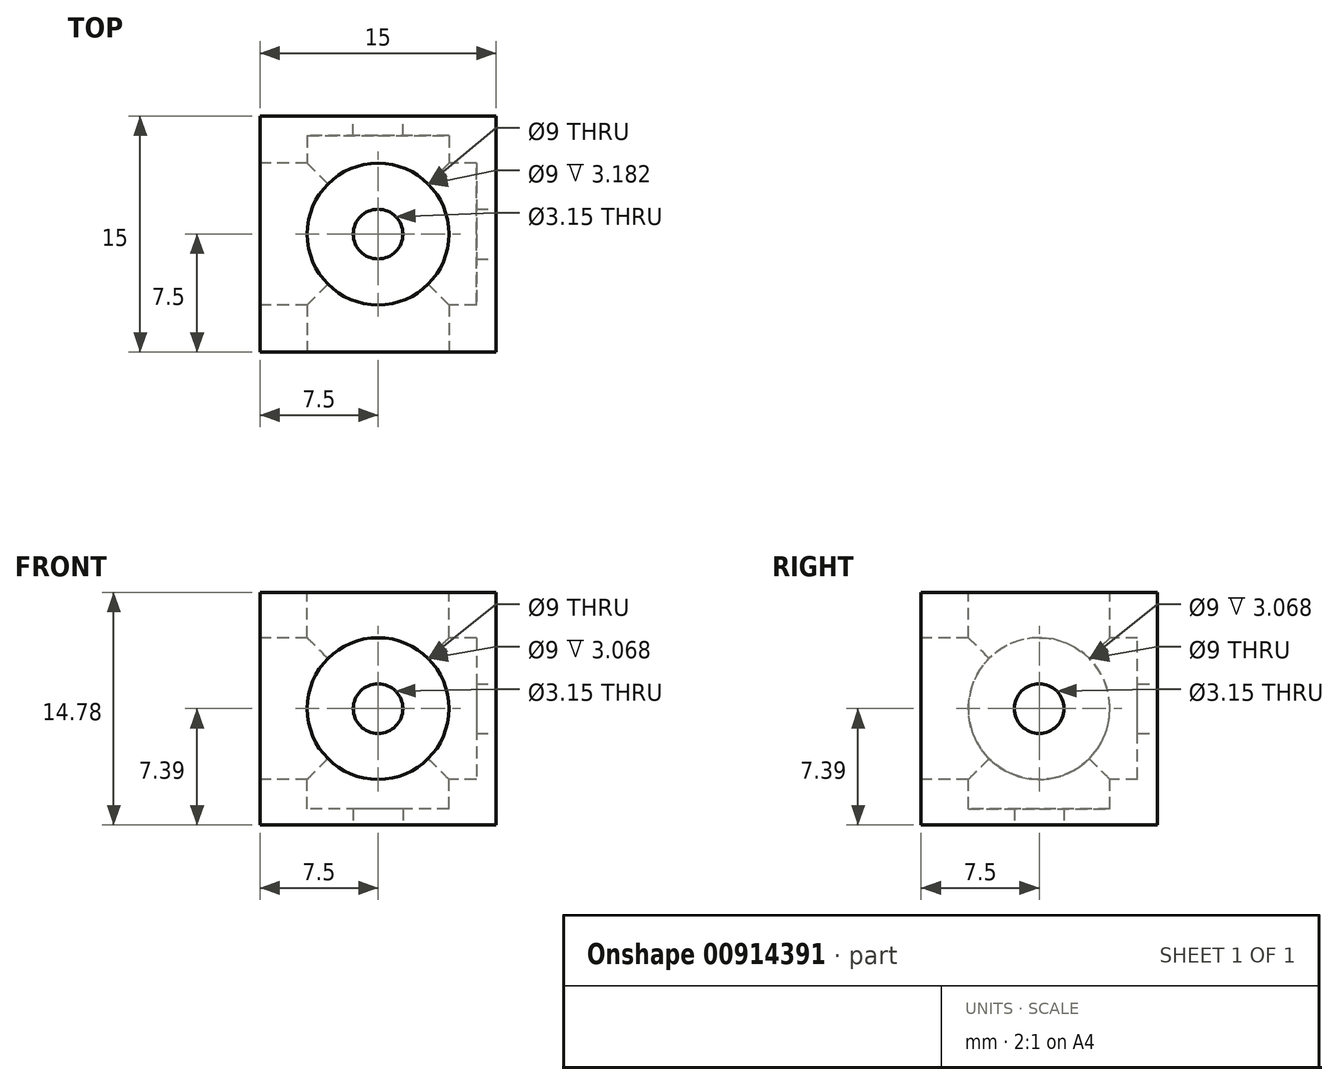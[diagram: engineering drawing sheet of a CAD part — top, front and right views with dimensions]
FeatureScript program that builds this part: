
annotation { "Feature Type Name" : "Feature", "Feature Type Description" : "" }
export const myFeature = defineFeature(function(context is Context, id is Id, definition is map)
    precondition{}
    {
        {
            var Q0;
            Q0=qCreatedBy(makeId("Front.planeOp"),FACE);
            var sketch = newSketch(context, id + "F0", { "sketchPlane" : qUnion([Q0])});
            skLineSegment(sketch, "E0.bottom", {"start": v(7.5, 7.39) * mm, "end": v(-7.5, 7.39) * mm});
            skLineSegment(sketch, "E0.top", {"start": v(7.5, -7.39) * mm, "end": v(-7.5, -7.39) * mm});
            skLineSegment(sketch, "E0.left", {"start": v(7.5, 7.39) * mm, "end": v(7.5, -7.39) * mm});
            skLineSegment(sketch, "E0.right", {"start": v(-7.5, 7.39) * mm, "end": v(-7.5, -7.39) * mm});
            skPoint(sketch, "E0.middle", {"position": v(0, 0) * mm});
            skSolve(sketch);
        }
        {
            var Q0;
            Q0=makeQuery(id+"F0.imprint","IMPRINT",FACE,{"disambiguationData":[TD([[makeQuery(id+"F0.imprint","IMPRINT",EDGE,{"derivedFrom":sQuery(id+"F0.wireOp",EDGE,"E0.bottom")}),1.0]])]});
            extrude(context, id + "F1", {"entities" : qUnion([Q0]), "depth" : 15 * mm, "offsetDistance" : 25 * mm});
        }
        {
            var Q0;
            Q0=makeQuery(id+"F1.opExtrude","CAP_FACE",FACE,{"disambiguationData":[OSD([sQuery(id+"F0.wireOp",EDGE,"E0.bottom"),sQuery(id+"F0.wireOp",EDGE,"E0.top"),sQuery(id+"F0.wireOp",EDGE,"E0.left"),sQuery(id+"F0.wireOp",EDGE,"E0.right")])],"isStart":false});
            var sketch = newSketch(context, id + "F2", { "sketchPlane" : qUnion([Q0])});
            skCircle(sketch, "E1", {"center": v(0, 0) * mm, "radius": 4.5 * mm});
            skSolve(sketch);
        }
        {
            var Q0;
            Q0=makeQuery(id+"F2.imprint","IMPRINT",FACE,{"disambiguationData":[TD([[makeQuery(id+"F2.imprint","IMPRINT",EDGE,{"derivedFrom":sQuery(id+"F2.wireOp",EDGE,"E1")}),1.0]])]});
            extrude(context, id + "F3", {"entities" : qUnion([Q0]), "operationType" : NewBodyOperationType.REMOVE, "oppositeDirection" : true, "depth" : 13.75 * mm, "offsetDistance" : 25 * mm});
        }
        {
            var Q0;
            Q0=makeQuery(id+"F1.opExtrude","SWEPT_FACE",FACE,{"disambiguationData":[OSD([sQuery(id+"F0.wireOp",EDGE,"E0.bottom")])]});
            var sketch = newSketch(context, id + "F4", { "sketchPlane" : qUnion([Q0])});
            skCircle(sketch, "E2", {"center": v(0, -7.5) * mm, "radius": 4.5 * mm});
            skPoint(sketch, "E2.centerSnap0", {"position": v(7.5, -7.5) * mm});
            skPoint(sketch, "E2.centerSnap1", {"position": v(0, -15) * mm});
            skSolve(sketch);
        }
        {
            var Q0;
            Q0=makeQuery(id+"F4.imprint","IMPRINT",FACE,{"disambiguationData":[TD([[makeQuery(id+"F4.imprint","IMPRINT",EDGE,{"derivedFrom":sQuery(id+"F4.wireOp",EDGE,"E2")}),1.0]])]});
            extrude(context, id + "F5", {"entities" : qUnion([Q0]), "operationType" : NewBodyOperationType.REMOVE, "oppositeDirection" : true, "depth" : 13.75 * mm, "offsetDistance" : 25 * mm});
        }
        {
            var Q0;
            Q0=makeQuery(id+"F1.opExtrude","SWEPT_FACE",FACE,{"disambiguationData":[OSD([sQuery(id+"F0.wireOp",EDGE,"E0.right")])]});
            var sketch = newSketch(context, id + "F6", { "sketchPlane" : qUnion([Q0])});
            skCircle(sketch, "E3", {"center": v(7.5, 0) * mm, "radius": 4.5 * mm});
            skPoint(sketch, "E3.centerSnap0", {"position": v(7.5, 7.39) * mm});
            skSolve(sketch);
        }
        {
            var Q0;
            Q0=makeQuery(id+"F6.imprint","IMPRINT",FACE,{"disambiguationData":[TD([[makeQuery(id+"F6.imprint","IMPRINT",EDGE,{"derivedFrom":sQuery(id+"F6.wireOp",EDGE,"E3")}),1.0]])]});
            extrude(context, id + "F7", {"entities" : qUnion([Q0]), "operationType" : NewBodyOperationType.REMOVE, "oppositeDirection" : true, "depth" : 13.75 * mm, "offsetDistance" : 25 * mm});
        }
        {
            var Q0;
            Q0=makeQuery(id+"F1.opExtrude","CAP_FACE",FACE,{"disambiguationData":[OSD([sQuery(id+"F0.wireOp",EDGE,"E0.bottom"),sQuery(id+"F0.wireOp",EDGE,"E0.top"),sQuery(id+"F0.wireOp",EDGE,"E0.left"),sQuery(id+"F0.wireOp",EDGE,"E0.right")])],"isStart":true});
            var sketch = newSketch(context, id + "F8", { "sketchPlane" : qUnion([Q0])});
            skCircle(sketch, "E4", {"center": v(0, 0) * mm, "radius": 1.57 * mm});
            skSolve(sketch);
        }
        {
            var Q0;
            Q0=makeQuery(id+"F8.imprint","IMPRINT",FACE,{"disambiguationData":[TD([[makeQuery(id+"F8.imprint","IMPRINT",EDGE,{"derivedFrom":sQuery(id+"F8.wireOp",EDGE,"E4")}),1.0]])]});
            extrude(context, id + "F9", {"entities" : qUnion([Q0]), "operationType" : NewBodyOperationType.REMOVE, "endBound" : BoundingType.THROUGH_ALL, "oppositeDirection" : true, "depth" : 25 * mm, "offsetDistance" : 25 * mm});
        }
        {
            var Q0;
            Q0=makeQuery(id+"F1.opExtrude","SWEPT_FACE",FACE,{"disambiguationData":[OSD([sQuery(id+"F0.wireOp",EDGE,"E0.top")])]});
            var sketch = newSketch(context, id + "F10", { "sketchPlane" : qUnion([Q0])});
            skCircle(sketch, "E5", {"center": v(0, 7.5) * mm, "radius": 1.57 * mm});
            skPoint(sketch, "E5.centerSnap0", {"position": v(-7.5, 7.5) * mm});
            skSolve(sketch);
        }
        {
            var Q0;
            Q0=qSketchRegion(id+"F10",true);
            extrude(context, id + "F11", {"entities" : qUnion([Q0]), "operationType" : NewBodyOperationType.REMOVE, "endBound" : BoundingType.THROUGH_ALL, "oppositeDirection" : true, "depth" : 25 * mm, "offsetDistance" : 25 * mm});
        }
        {
            var Q0;
            Q0=makeQuery(id+"F1.opExtrude","SWEPT_FACE",FACE,{"disambiguationData":[OSD([sQuery(id+"F0.wireOp",EDGE,"E0.left")])]});
            var sketch = newSketch(context, id + "F12", { "sketchPlane" : qUnion([Q0])});
            skCircle(sketch, "E6", {"center": v(-7.5, 0) * mm, "radius": 1.57 * mm});
            skPoint(sketch, "E6.centerSnap0", {"position": v(-7.5, -7.39) * mm});
            skSolve(sketch);
        }
        {
            var Q0;
            Q0=qSketchRegion(id+"F12",true);
            extrude(context, id + "F13", {"entities" : qUnion([Q0]), "operationType" : NewBodyOperationType.REMOVE, "endBound" : BoundingType.THROUGH_ALL, "oppositeDirection" : true, "depth" : 25 * mm, "offsetDistance" : 25 * mm});
        }
    });
